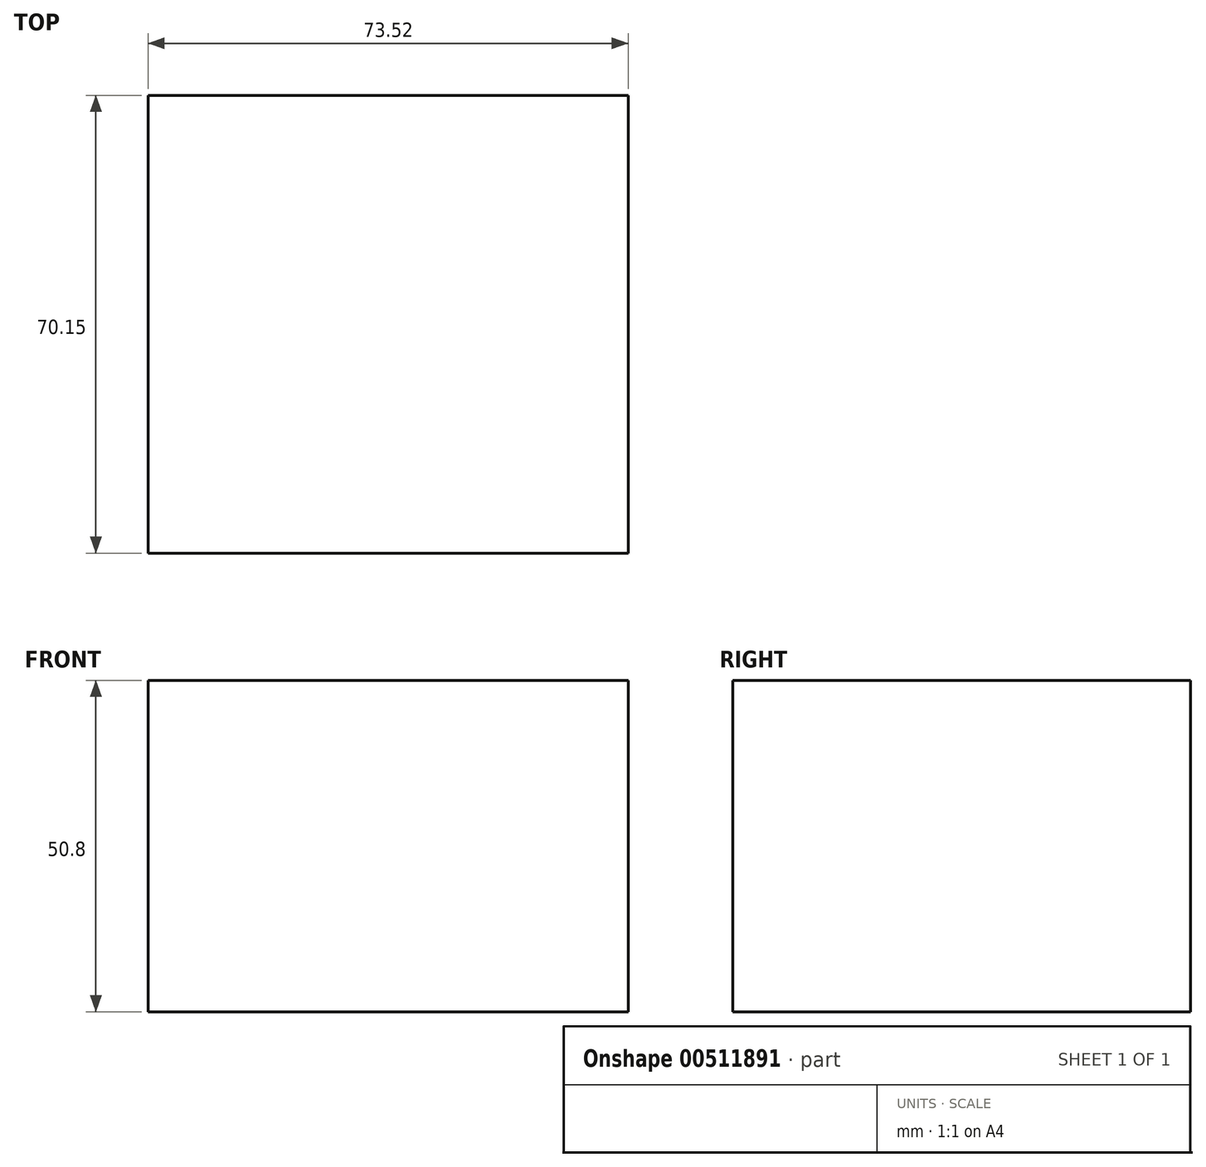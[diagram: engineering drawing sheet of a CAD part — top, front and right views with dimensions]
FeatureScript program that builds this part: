
annotation { "Feature Type Name" : "Feature", "Feature Type Description" : "" }
export const myFeature = defineFeature(function(context is Context, id is Id, definition is map)
    precondition{}
    {
        {
            var Q0;
            Q0=qCreatedBy(makeId("Top.planeOp"),FACE);
            var sketch = newSketch(context, id + "F0", { "sketchPlane" : qUnion([Q0])});
            skLineSegment(sketch, "E0.bottom", {"start": v(-609.6, 228.6) * mm, "end": v(609.6, 228.6) * mm});
            skLineSegment(sketch, "E0.top", {"start": v(-609.6, -228.6) * mm, "end": v(609.6, -228.6) * mm});
            skLineSegment(sketch, "E0.left", {"start": v(-609.6, 228.6) * mm, "end": v(-609.6, -228.6) * mm});
            skLineSegment(sketch, "E0.right", {"start": v(609.6, 228.6) * mm, "end": v(609.6, -228.6) * mm});
            skPoint(sketch, "E0.middle", {"position": v(0, 0) * mm});
            skSolve(sketch);
        }
        {
            var Q0;
            Q0=qCreatedBy(makeId("Front.planeOp"),FACE);
            var Q1;
            Q1=sQuery(id+"F0.wireOp",VERTEX,"E0.top.end");
            cPlane(context, id + "F1", {"entities" : qUnion([Q0, Q1]), "cplaneType" : CPlaneType.PLANE_POINT, "offset" : 25.4 * mm, "width" : 152.4 * mm, "height" : 152.4 * mm});
        }
        {
            var Q0;
            Q0=qCreatedBy(id+"F1.planeOp",FACE);
            var sketch = newSketch(context, id + "F2", { "sketchPlane" : qUnion([Q0])});
            skLineSegment(sketch, "E1.bottom", {"start": v(609.6, 0) * mm, "end": v(-609.6, 0) * mm});
            skLineSegment(sketch, "E1.top", {"start": v(609.6, -406.4) * mm, "end": v(-609.6, -406.4) * mm});
            skLineSegment(sketch, "E1.left", {"start": v(609.6, 0) * mm, "end": v(609.6, -406.4) * mm});
            skLineSegment(sketch, "E1.right", {"start": v(-609.6, 0) * mm, "end": v(-609.6, -406.4) * mm});
            skSolve(sketch);
        }
        {
            var Q0;
            Q0=makeQuery(id+"F0.imprint","IMPRINT",FACE,{"disambiguationData":[TD([[makeQuery(id+"F0.imprint","IMPRINT",EDGE,{"derivedFrom":sQuery(id+"F0.wireOp",EDGE,"E0.bottom")}),-1.0]])]});
            var sketch = newSketch(context, id + "F3", { "sketchPlane" : qUnion([Q0])});
            skCircle(sketch, "E2", {"center": v(608.96, -227.28) * mm, "radius": 25.4 * mm});
            skSolve(sketch);
        }
        {
            var Q0;
            Q0 = qSketchRegion(id + "F0", true);
            var sketch = newSketch(context, id + "F4", { "sketchPlane" : qUnion([Q0])});
            skLineSegment(sketch, "E3.bottom", {"start": v(647.1, -187.38) * mm, "end": v(573.6, -187.38) * mm});
            skLineSegment(sketch, "E3.top", {"start": v(647.1, -257.53) * mm, "end": v(573.6, -257.53) * mm});
            skLineSegment(sketch, "E3.left", {"start": v(647.1, -187.38) * mm, "end": v(647.1, -257.53) * mm});
            skLineSegment(sketch, "E3.right", {"start": v(573.6, -187.38) * mm, "end": v(573.6, -257.53) * mm});
            skPoint(sketch, "E3.middle", {"position": v(610.35, -222.46) * mm, "construction": true});
            skSolve(sketch);
        }
        {
            var Q0;
            Q0 = qSketchRegion(id + "FqaDGAQg7U6BVw7_1", true);
            var Q1;
            Q1 = qSketchRegion(id + "F4", true);
            extrude(context, id + "F5", {"entities" : qUnion([Q0, Q1]), "domain" : OperationDomain.MODEL, "flatOperationType" : FlatOperationType.REMOVE, "depth" : 50.8 * mm, "offsetDistance" : 25.4 * mm});
        }
    });
